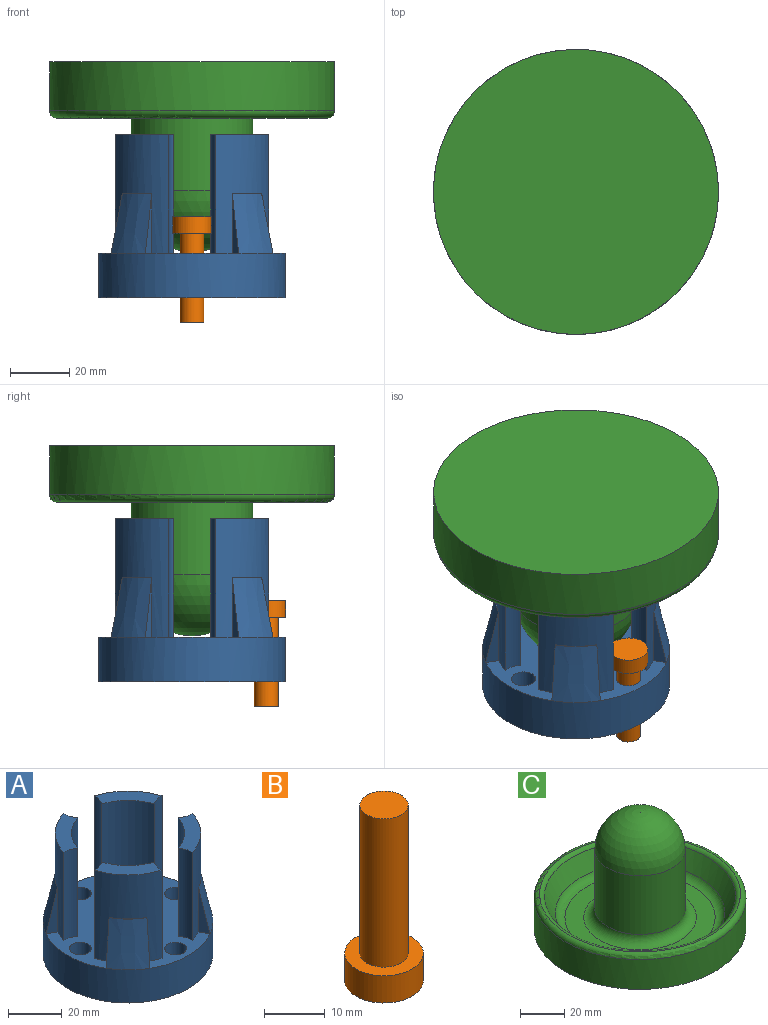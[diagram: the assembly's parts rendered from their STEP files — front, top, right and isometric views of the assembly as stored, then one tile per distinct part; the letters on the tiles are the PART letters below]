
ASSEMBLY  parts=3 mates=2
PART A: 45 faces, bbox 63x63x55 mm
  f0: plane 20x3.9mm, normal (0.5,-0.87,0), area 46mm2, adj f10,f12,f31,f44
  f1: plane 20x3.9mm, normal (-0.87,0.5,0), area 46mm2, adj f10,f12,f31,f44
  f2: plane 20x3.9mm, normal (0.87,0.5,0), area 46mm2, adj f10,f11,f32,f43
  f3: plane 20x3.9mm, normal (-0.5,-0.87,0), area 46mm2, adj f10,f11,f32,f43
  f4: plane 20x3.9mm, normal (-0.5,0.87,0), area 46mm2, adj f9,f10,f33,f42
  f5: plane 20x3.9mm, normal (0.87,-0.5,0), area 46mm2, adj f9,f10,f33,f42
  f6: plane 20x3.9mm, normal (-0.87,-0.5,0), area 46mm2, adj f8,f10,f34,f41
  f7: plane 20x3.9mm, normal (0.5,0.87,0), area 46mm2, adj f8,f10,f34,f41
  f8: cylinder r=27mm len=40mm, axis (0,0,-1), area 767.3mm2, adj f6,f7,f10,f27,f28,f30,f34
  f9: cylinder r=27mm len=40mm, axis (0,0,-1), area 767.3mm2, adj f4,f5,f10,f23,f24,f26,f33
  f10: plane 63x63mm, normal (0,0,1), area 2094.4mm2, adj f0,f1,f2,f3,f4,f5,f6,f7
  f11: cylinder r=27mm len=40mm, axis (0,0,-1), area 767.3mm2, adj f2,f3,f10,f15,f16,f18,f32
  f12: cylinder r=27mm len=40mm, axis (0,0,-1), area 767.3mm2, adj f0,f1,f10,f19,f21,f22,f31
  f13: cylinder r=31.5mm len=63mm, axis (0,0,1), area 2968.8mm2, adj f10,f14,f41,f42,f43,f44
  f14: plane 63x63mm, normal (0,0,-1), area 2911.1mm2, adj f13,f37,f38,f39,f40
  f15: cylinder r=8mm len=40mm, axis (0,0,-1), area 246.1mm2, adj f10,f11,f17,f18
  f16: cylinder r=8mm len=40mm, axis (0,0,-1), area 246.1mm2, adj f10,f11,f17,f18
  f17: cylinder r=21mm len=40mm, axis (0,0,-1), area 809.5mm2, adj f10,f15,f16,f18
  f18: plane 19.52x19.52mm, normal (0,0,1), area 134.8mm2, adj f11,f15,f16,f17
  f19: cylinder r=8mm len=40mm, axis (0,0,-1), area 246.1mm2, adj f10,f12,f20,f22
  f20: cylinder r=21mm len=40mm, axis (0,0,-1), area 809.5mm2, adj f10,f19,f21,f22
  f21: cylinder r=8mm len=40mm, axis (0,0,-1), area 246.1mm2, adj f10,f12,f20,f22
  f22: plane 19.52x19.52mm, normal (0,0,1), area 134.8mm2, adj f12,f19,f20,f21
  f23: cylinder r=8mm len=40mm, axis (0,0,-1), area 246.1mm2, adj f9,f10,f25,f26
  f24: cylinder r=8mm len=40mm, axis (0,0,-1), area 246.1mm2, adj f9,f10,f25,f26
  f25: cylinder r=21mm len=40mm, axis (0,0,-1), area 809.5mm2, adj f10,f23,f24,f26
  f26: plane 19.52x19.52mm, normal (0,0,1), area 134.8mm2, adj f9,f23,f24,f25
  f27: cylinder r=8mm len=40mm, axis (0,0,-1), area 246.1mm2, adj f8,f10,f29,f30
  f28: cylinder r=8mm len=40mm, axis (0,0,-1), area 246.1mm2, adj f8,f10,f29,f30
  f29: cylinder r=21mm len=40mm, axis (0,0,-1), area 809.5mm2, adj f10,f27,f28,f30
  f30: plane 19.52x19.52mm, normal (0,0,1), area 134.8mm2, adj f8,f27,f28,f29
  f31: plane 9.97x9.97mm, normal (0,0,1), area 1.4mm2, adj f0,f1,f12,f44
  f32: plane 9.97x9.97mm, normal (0,0,1), area 1.4mm2, adj f2,f3,f11,f43
  f33: plane 9.97x9.97mm, normal (0,0,1), area 1.4mm2, adj f4,f5,f9,f42
  f34: plane 9.97x9.97mm, normal (0,0,1), area 1.4mm2, adj f6,f7,f8,f41
  f35: cylinder r=0.8mm len=6mm, axis (0,0,1), area 30.2mm2, adj f10,f36
  f36: plane 1.6x1.6mm, normal (0,0,1), area 2mm2, adj f35
  f37: cylinder r=4.05mm len=15mm, axis (0,0,1), area 381.7mm2, adj f10,f14
  f38: cylinder r=4.05mm len=15mm, axis (0,0,1), area 381.7mm2, adj f10,f14
  f39: cylinder r=4.05mm len=15mm, axis (0,0,1), area 381.7mm2, adj f10,f14
  f40: cylinder r=4.05mm len=15mm, axis (0,0,1), area 381.7mm2, adj f10,f14
  f41: cone r=27.1mm half-angle=12.4deg, axis (0,0,-1), area 314.2mm2, adj f6,f7,f13,f34
  f42: cone r=27.1mm half-angle=12.4deg, axis (0,0,-1), area 314.2mm2, adj f4,f5,f13,f33
  f43: cone r=27.1mm half-angle=12.4deg, axis (0,0,-1), area 314.2mm2, adj f2,f3,f13,f32
  f44: cone r=27.1mm half-angle=12.4deg, axis (0,0,-1), area 314.2mm2, adj f0,f1,f13,f31
PART B: 5 faces, bbox 13x13x35.5 mm
  f0: plane 13x13mm, normal (0,0,1), area 82.5mm2, adj f1,f4
  f1: cylinder r=4mm len=30mm, axis (0,0,-1), area 754mm2, adj f0,f2
  f2: plane 8x8mm, normal (0,0,1), area 50.3mm2, adj f1
  f3: plane 13x13mm, normal (0,0,-1), area 132.7mm2, adj f4
  f4: cylinder r=6.5mm len=13mm, axis (0,0,-1), area 224.6mm2, adj f0,f3
PART C: 11 faces, bbox 103.9x103.9x64 mm
  f0: cylinder r=20.5mm len=41mm, axis (0,0,1), area 4186.2mm2, adj f1,f10
  f1: sphere r=20.5mm, area 2640.5mm2, adj f0
  f2: plane 96x96mm, normal (0,0,-1), area 7238.2mm2, adj f3
  f3: cylinder r=48mm len=96mm, axis (0,0,1), area 4976.3mm2, adj f2,f7
  f4: plane 91x91mm, normal (0,0,1), area 1.9mm2, adj f7,f8
  f5: cone r=44mm half-angle=28.3deg, axis (0,0,1), area 2640.1mm2, adj f8,f9
  f6: plane 68.03x68.03mm, normal (0,0,1), area 1591.8mm2, adj f9,f10
  f7: torus R=45.5mm, axis (0,0,-1), area 1161.9mm2, adj f3,f4
  f8: torus R=45.49mm, axis (0,0,-1), area 748.9mm2, adj f4,f5
  f9: torus R=34.01mm, axis (0,0,1), area 1233.3mm2, adj f5,f6
  f10: torus R=25.5mm, axis (0,0,1), area 1101.3mm2, adj f0,f6
PLACE A rot(axis=(0,0,-1),0deg) t=(-78.31,-109.31,4.24)mm
PLACE B rot(axis=(-1,0,0),180deg) t=(-78.31,-134.31,11.02)mm
PLACE C rot(axis=(-1,0,0),180deg) t=(-78.31,-109.31,59.24)mm
MATE revolute C.f5 <-> A.f8  axis (0,0,-1) through (-78.31,-109.31,25.24)mm
MATE slider B.f1 <-> A.f38  axis (0,0,1) through (-78.31,-134.31,11.02)mm
